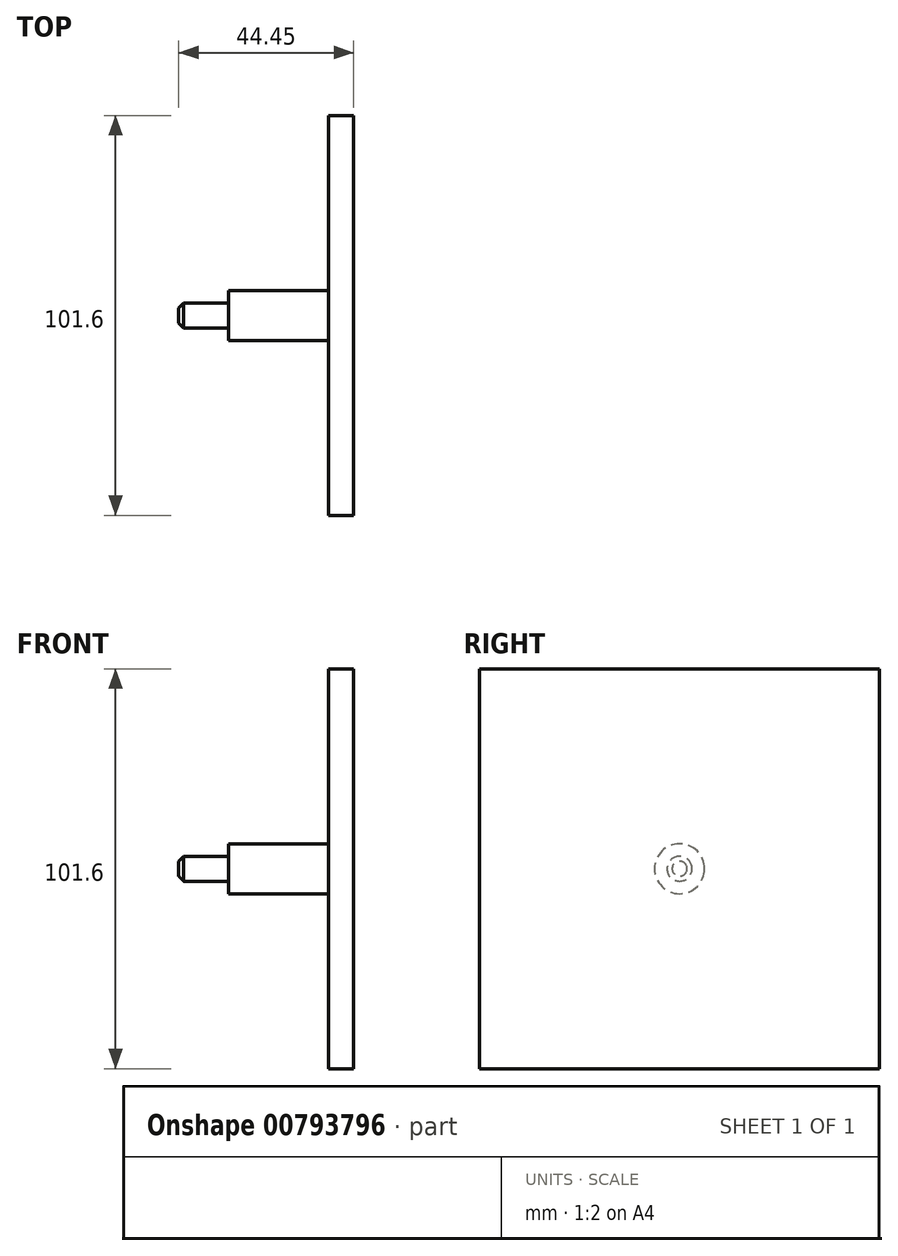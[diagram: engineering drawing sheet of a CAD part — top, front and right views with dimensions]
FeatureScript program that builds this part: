
annotation { "Feature Type Name" : "Feature", "Feature Type Description" : "" }
export const myFeature = defineFeature(function(context is Context, id is Id, definition is map)
    precondition{}
    {
        {
            var Q0;
            Q0=qCreatedBy(makeId("Right.planeOp"),FACE);
            var sketch = newSketch(context, id + "F0", { "sketchPlane" : qUnion([Q0])});
            skCircle(sketch, "E0", {"center": v(0, 0) * mm, "radius": 3.18 * mm});
            skSolve(sketch);
        }
        {
            var Q0;
            Q0 = qSketchRegion(id + "F0", true);
            extrude(context, id + "F1", {"entities" : qUnion([Q0]), "depth" : 12.7 * mm, "offsetDistance" : 25.4 * mm});
        }
        {
            var Q0;
            Q0=makeQuery(id+"F1.opExtrude","CAP_EDGE",EDGE,{"disambiguationData":[OSD([sQuery(id+"F0.wireOp",EDGE,"E0")])],"isStart":true});
            chamfer(context, id + "F2", {"entities" : qUnion([Q0]), "width" : 1.27 * mm, "tangentPropagation" : true});
        }
        {
            var Q0;
            Q0=makeQuery(id+"F1.opExtrude","CAP_FACE",FACE,{"disambiguationData":[OSD([sQuery(id+"F0.wireOp",EDGE,"E0")])],"isStart":false});
            var sketch = newSketch(context, id + "F3", { "sketchPlane" : qUnion([Q0])});
            skCircle(sketch, "E1", {"center": v(0, 0) * mm, "radius": 6.35 * mm});
            skSolve(sketch);
        }
        {
            var Q0;
            Q0 = qSketchRegion(id + "F3", true);
            extrude(context, id + "F4", {"entities" : qUnion([Q0]), "operationType" : NewBodyOperationType.ADD, "depth" : 25.4 * mm, "offsetDistance" : 25.4 * mm});
        }
        {
            var Q0;
            Q0=makeQuery(id+"F4.opExtrude","CAP_FACE",FACE,{"disambiguationData":[OSD([sQuery(id+"F3.wireOp",EDGE,"E1")])],"isStart":false});
            var sketch = newSketch(context, id + "F5", { "sketchPlane" : qUnion([Q0])});
            skLineSegment(sketch, "E2.bottom", {"start": v(-50.8, 50.8) * mm, "end": v(50.8, 50.8) * mm});
            skLineSegment(sketch, "E2.top", {"start": v(-50.8, -50.8) * mm, "end": v(50.8, -50.8) * mm});
            skLineSegment(sketch, "E2.left", {"start": v(-50.8, 50.8) * mm, "end": v(-50.8, -50.8) * mm});
            skLineSegment(sketch, "E2.right", {"start": v(50.8, 50.8) * mm, "end": v(50.8, -50.8) * mm});
            skPoint(sketch, "E2.middle", {"position": v(0, 0) * mm});
            skSolve(sketch);
        }
        {
            var Q0;
            Q0=makeQuery(id+"F5.imprint","IMPRINT",FACE,{"disambiguationData":[TD([[makeQuery(id+"F5.imprint","IMPRINT",EDGE,{"derivedFrom":makeQuery(id+"F4.opExtrude","CAP_EDGE",EDGE,{"disambiguationData":[OSD([sQuery(id+"F3.wireOp",EDGE,"E1")])],"isStart":false})}),1.0]])]});
            var Q1;
            Q1=makeQuery(id+"F5.imprint","IMPRINT",FACE,{"disambiguationData":[TD([[makeQuery(id+"F5.imprint","IMPRINT",EDGE,{"derivedFrom":sQuery(id+"F5.wireOp",EDGE,"E2.bottom")}),-1.0]])]});
            extrude(context, id + "F6", {"entities" : qUnion([Q0, Q1]), "operationType" : NewBodyOperationType.ADD, "depth" : 6.35 * mm, "offsetDistance" : 25.4 * mm});
        }
    });
